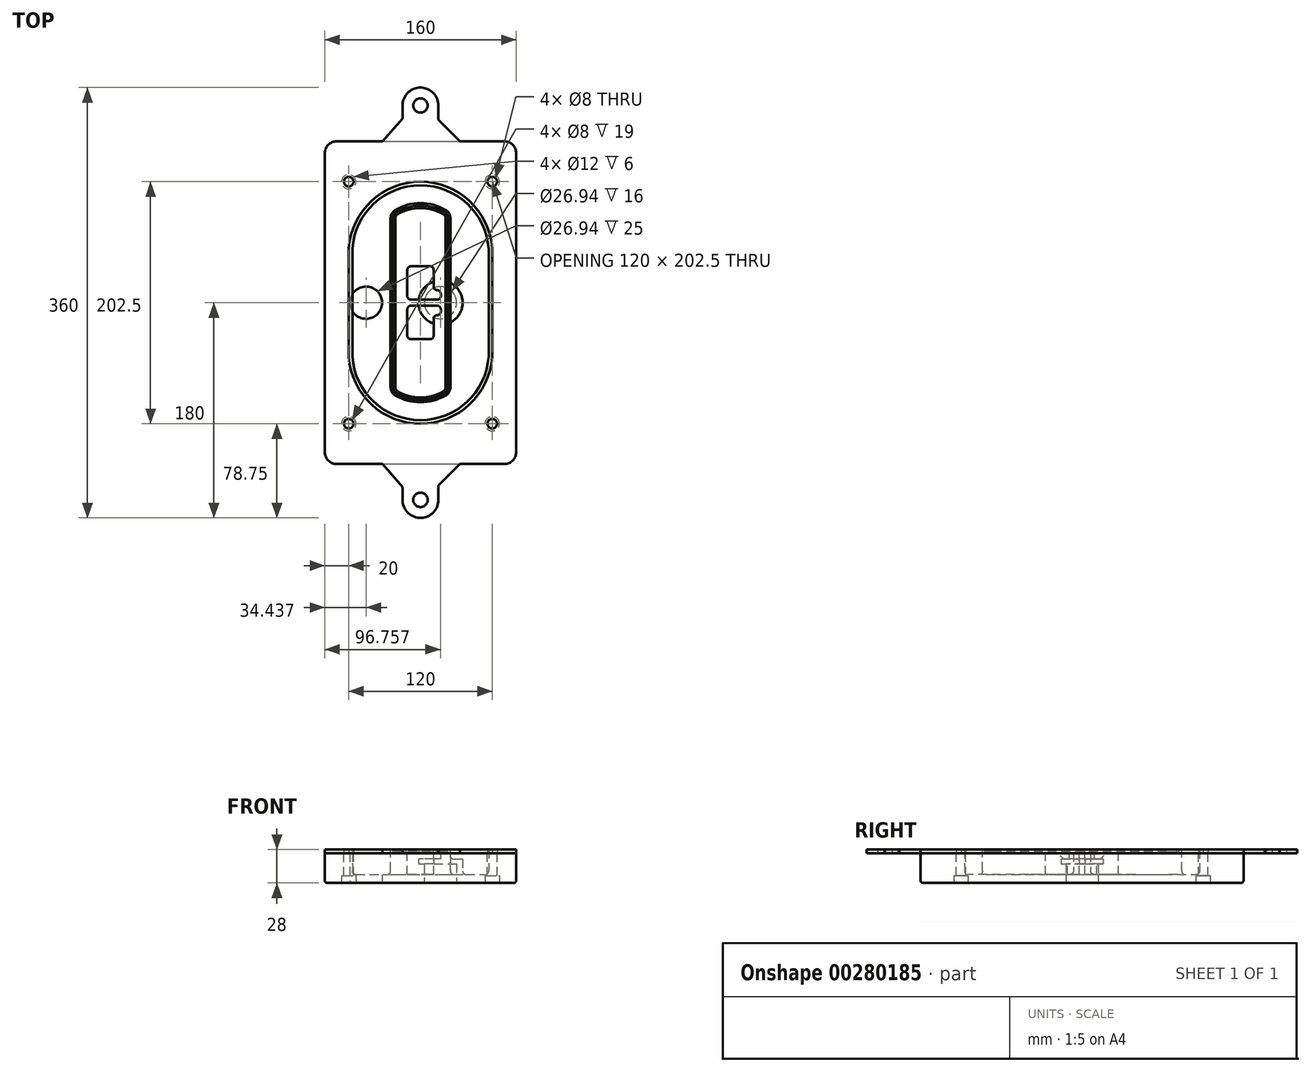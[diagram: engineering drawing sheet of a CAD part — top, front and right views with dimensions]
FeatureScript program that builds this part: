
annotation { "Feature Type Name" : "Feature", "Feature Type Description" : "" }
export const myFeature = defineFeature(function(context is Context, id is Id, definition is map)
    precondition{}
    {
        {
            var Q0;
            Q0=qCreatedBy(makeId("Top.planeOp"),FACE);
            var sketch = newSketch(context, id + "F0", { "sketchPlane" : qUnion([Q0])});
            skPoint(sketch, "E0.rect.middle", {"position": v(0, 0) * mm});
            skLineSegment(sketch, "E1.bottom", {"start": v(-70, -135) * mm, "end": v(70, -135) * mm});
            skLineSegment(sketch, "E1.top", {"start": v(-70, 135) * mm, "end": v(70, 135) * mm});
            skLineSegment(sketch, "E1.left", {"start": v(-80, -125) * mm, "end": v(-80, 125) * mm});
            skLineSegment(sketch, "E1.right", {"start": v(80, -125) * mm, "end": v(80, 125) * mm});
            skLineSegment(sketch, "E2", {"start": v(-80, 135) * mm, "end": v(80, -135) * mm, "construction": true});
            skLineSegment(sketch, "E3", {"start": v(80, 135) * mm, "end": v(-80, -135) * mm, "construction": true});
            skCircle(sketch, "E4", {"center": v(-60, 101.25) * mm, "radius": 4 * mm});
            skCircle(sketch, "E5", {"center": v(60, 101.25) * mm, "radius": 4 * mm});
            skCircle(sketch, "E6", {"center": v(60, -101.25) * mm, "radius": 4 * mm});
            skCircle(sketch, "E7", {"center": v(-60, -101.25) * mm, "radius": 4 * mm});
            skLineSegment(sketch, "E8", {"start": v(-60, 101.25) * mm, "end": v(60, 101.25) * mm, "construction": true});
            skLineSegment(sketch, "E9", {"start": v(60, 101.25) * mm, "end": v(60, -101.25) * mm, "construction": true});
            skLineSegment(sketch, "E10", {"start": v(60, -101.25) * mm, "end": v(-60, -101.25) * mm, "construction": true});
            skLineSegment(sketch, "E11", {"start": v(-60, -101.25) * mm, "end": v(-60, 101.25) * mm, "construction": true});
            skLineSegment(sketch, "E12", {"start": v(-60, 44.66) * mm, "end": v(-60, -44.66) * mm});
            skLineSegment(sketch, "E13", {"start": v(60, 44.66) * mm, "end": v(60, -44.66) * mm});
            skArc(sketch, "E14", {"start": v(59.98, 45.37) * mm, "mid": v(0, 101.25) * mm, "end": v(-59.98, 45.37) * mm});
            skArc(sketch, "E15", {"start": v(-59.98, -45.37) * mm, "mid": v(0, -101.25) * mm, "end": v(59.98, -45.37) * mm});
            skLineSegment(sketch, "E16", {"start": v(-60, 0) * mm, "end": v(60, 0) * mm, "construction": true});
            skPoint(sketch, "E17.visualSharp", {"position": v(-60, -45) * mm});
            skArc(sketch, "E17.filletArc", {"start": v(-60, -44.66) * mm, "mid": v(-60, -45.02) * mm, "end": v(-59.98, -45.37) * mm});
            skPoint(sketch, "E18.visualSharp", {"position": v(-60, 45) * mm});
            skArc(sketch, "E18.filletArc", {"start": v(-59.98, 45.37) * mm, "mid": v(-60, 45.02) * mm, "end": v(-60, 44.66) * mm});
            skPoint(sketch, "E19.visualSharp", {"position": v(60, 45) * mm});
            skArc(sketch, "E19.filletArc", {"start": v(60, 44.66) * mm, "mid": v(60, 45.02) * mm, "end": v(59.98, 45.37) * mm});
            skPoint(sketch, "E20.visualSharp", {"position": v(60, -45) * mm});
            skArc(sketch, "E20.filletArc", {"start": v(59.98, -45.37) * mm, "mid": v(60, -45.02) * mm, "end": v(60, -44.66) * mm});
            skPoint(sketch, "E21.visualSharp", {"position": v(-80, 135) * mm});
            skArc(sketch, "E21.filletArc", {"start": v(-70, 135) * mm, "mid": v(-77.07, 132.07) * mm, "end": v(-80, 125) * mm});
            skPoint(sketch, "E22.visualSharp", {"position": v(80, 135) * mm});
            skArc(sketch, "E22.filletArc", {"start": v(80, 125) * mm, "mid": v(77.07, 132.07) * mm, "end": v(70, 135) * mm});
            skPoint(sketch, "E23.visualSharp", {"position": v(80, -135) * mm});
            skArc(sketch, "E23.filletArc", {"start": v(70, -135) * mm, "mid": v(77.07, -132.07) * mm, "end": v(80, -125) * mm});
            skPoint(sketch, "E24.visualSharp", {"position": v(-80, -135) * mm});
            skArc(sketch, "E24.filletArc", {"start": v(-80, -125) * mm, "mid": v(-77.07, -132.07) * mm, "end": v(-70, -135) * mm});
            skArc(sketch, "E25.0", {"start": v(57, 44.66) * mm, "mid": v(57, 44.9) * mm, "end": v(56.98, 45.16) * mm});
            skLineSegment(sketch, "E25.1", {"start": v(57, 44.66) * mm, "end": v(57, -44.66) * mm});
            skArc(sketch, "E25.2", {"start": v(56.98, -45.16) * mm, "mid": v(57, -44.9) * mm, "end": v(57, -44.66) * mm});
            skArc(sketch, "E25.3", {"start": v(-56.98, -45.16) * mm, "mid": v(0, -98.25) * mm, "end": v(56.98, -45.16) * mm});
            skArc(sketch, "E25.4", {"start": v(-57, -44.66) * mm, "mid": v(-57, -44.9) * mm, "end": v(-56.98, -45.16) * mm});
            skArc(sketch, "E25.5", {"start": v(56.98, 45.16) * mm, "mid": v(0, 98.25) * mm, "end": v(-56.98, 45.16) * mm});
            skLineSegment(sketch, "E25.6", {"start": v(-57, 44.66) * mm, "end": v(-57, -44.66) * mm});
            skArc(sketch, "E25.7", {"start": v(-56.98, 45.16) * mm, "mid": v(-57, 44.9) * mm, "end": v(-57, 44.66) * mm});
            skArc(sketch, "E26.0", {"start": v(-63.97, 45.65) * mm, "mid": v(-64, 45.16) * mm, "end": v(-64, 44.66) * mm});
            skArc(sketch, "E26.1", {"start": v(63.97, 45.65) * mm, "mid": v(0, 105.25) * mm, "end": v(-63.97, 45.65) * mm});
            skArc(sketch, "E26.2", {"start": v(64, 44.66) * mm, "mid": v(64, 45.16) * mm, "end": v(63.97, 45.65) * mm});
            skLineSegment(sketch, "E26.3", {"start": v(64, 44.66) * mm, "end": v(64, -44.66) * mm});
            skArc(sketch, "E26.4", {"start": v(63.97, -45.65) * mm, "mid": v(64, -45.16) * mm, "end": v(64, -44.66) * mm});
            skLineSegment(sketch, "E26.5", {"start": v(-64, 44.66) * mm, "end": v(-64, -44.66) * mm});
            skArc(sketch, "E26.6", {"start": v(-63.97, -45.65) * mm, "mid": v(0, -105.25) * mm, "end": v(63.97, -45.65) * mm});
            skArc(sketch, "E26.7", {"start": v(-64, -44.66) * mm, "mid": v(-64, -45.16) * mm, "end": v(-63.97, -45.65) * mm});
            skSolve(sketch);
        }
        {
            var Q0;
            Q0=makeQuery(id+"F0.imprint","IMPRINT",FACE,{"disambiguationData":[TD([[makeQuery(id+"F0.imprint","IMPRINT",EDGE,{"derivedFrom":sQuery(id+"F0.wireOp",EDGE,"E1.bottom")}),1.0]])]});
            var Q1;
            Q1=makeQuery(id+"F0.imprint","IMPRINT",FACE,{"disambiguationData":[TD([[makeQuery(id+"F0.imprint","IMPRINT",EDGE,{"derivedFrom":sQuery(id+"F0.wireOp",EDGE,"E12")}),1.0]])]});
            var Q2;
            Q2=makeQuery(id+"F0.imprint","IMPRINT",FACE,{"disambiguationData":[TD([[makeQuery(id+"F0.imprint","IMPRINT",EDGE,{"derivedFrom":sQuery(id+"F0.wireOp",EDGE,"E25.0")}),1.0]])]});
            var Q3;
            Q3=makeQuery(id+"F0.imprint","IMPRINT",FACE,{"disambiguationData":[TD([[makeQuery(id+"F0.imprint","IMPRINT",EDGE,{"derivedFrom":sQuery(id+"F0.wireOp",EDGE,"E12")}),-1.0]])]});
            extrude(context, id + "F1", {"entities" : qUnion([Q0, Q1, Q2, Q3]), "oppositeDirection" : true, "depth" : 25 * mm});
        }
        {
            var Q0;
            Q0=makeQuery(id+"F0.imprint","IMPRINT",FACE,{"disambiguationData":[TD([[makeQuery(id+"F0.imprint","IMPRINT",EDGE,{"derivedFrom":sQuery(id+"F0.wireOp",EDGE,"E12")}),1.0]])]});
            extrude(context, id + "F2", {"entities" : qUnion([Q0]), "operationType" : NewBodyOperationType.ADD, "depth" : 3 * mm});
        }
        {
            var Q0;
            Q0=makeQuery(id+"F0.imprint","IMPRINT",FACE,{"disambiguationData":[TD([[makeQuery(id+"F0.imprint","IMPRINT",EDGE,{"derivedFrom":sQuery(id+"F0.wireOp",EDGE,"E25.0")}),1.0]])]});
            extrude(context, id + "F3", {"entities" : qUnion([Q0]), "operationType" : NewBodyOperationType.REMOVE, "oppositeDirection" : true, "depth" : 18 * mm});
        }
        {
            var Q0;
            Q0=makeQuery(id+"F2.opExtrude","CAP_FACE",FACE,{"disambiguationData":[OSD([sQuery(id+"F0.wireOp",EDGE,"E12"),sQuery(id+"F0.wireOp",EDGE,"E13"),sQuery(id+"F0.wireOp",EDGE,"E14"),sQuery(id+"F0.wireOp",EDGE,"E15"),sQuery(id+"F0.wireOp",EDGE,"E17.filletArc"),sQuery(id+"F0.wireOp",EDGE,"E18.filletArc"),sQuery(id+"F0.wireOp",EDGE,"E19.filletArc"),sQuery(id+"F0.wireOp",EDGE,"E20.filletArc"),sQuery(id+"F0.wireOp",EDGE,"E25.0"),sQuery(id+"F0.wireOp",EDGE,"E25.1"),sQuery(id+"F0.wireOp",EDGE,"E25.2"),sQuery(id+"F0.wireOp",EDGE,"E25.3"),sQuery(id+"F0.wireOp",EDGE,"E25.4"),sQuery(id+"F0.wireOp",EDGE,"E25.5"),sQuery(id+"F0.wireOp",EDGE,"E25.6"),sQuery(id+"F0.wireOp",EDGE,"E25.7")])],"isStart":false});
            var sketch = newSketch(context, id + "F4", { "sketchPlane" : qUnion([Q0])});
            skArc(sketch, "E27.0", {"start": v(-20.99, -77.65) * mm, "mid": v(0, -83.25) * mm, "end": v(20.99, -77.65) * mm});
            skArc(sketch, "E28.0", {"start": v(20.99, 77.65) * mm, "mid": v(0, 83.25) * mm, "end": v(-20.99, 77.65) * mm});
            skLineSegment(sketch, "E29", {"start": v(-25, 70.71) * mm, "end": v(-25, -70.71) * mm});
            skLineSegment(sketch, "E30", {"start": v(25, 70.71) * mm, "end": v(25, -70.71) * mm});
            skLineSegment(sketch, "E31", {"start": v(-25, 75.03) * mm, "end": v(25, 75.03) * mm, "construction": true});
            skLineSegment(sketch, "E32", {"start": v(-25, -75.03) * mm, "end": v(25, -75.03) * mm, "construction": true});
            skPoint(sketch, "E33.visualSharp", {"position": v(-25, 75.03) * mm});
            skArc(sketch, "E33.filletArc", {"start": v(-20.99, 77.65) * mm, "mid": v(-23.92, 74.72) * mm, "end": v(-25, 70.71) * mm});
            skPoint(sketch, "E34.visualSharp", {"position": v(25, 75.03) * mm});
            skArc(sketch, "E34.filletArc", {"start": v(25, 70.71) * mm, "mid": v(23.92, 74.72) * mm, "end": v(20.99, 77.65) * mm});
            skPoint(sketch, "E35.visualSharp", {"position": v(25, -75.03) * mm});
            skArc(sketch, "E35.filletArc", {"start": v(20.99, -77.65) * mm, "mid": v(23.92, -74.72) * mm, "end": v(25, -70.71) * mm});
            skPoint(sketch, "E36.visualSharp", {"position": v(-25, -75.03) * mm});
            skArc(sketch, "E36.filletArc", {"start": v(-25, -70.71) * mm, "mid": v(-23.92, -74.72) * mm, "end": v(-20.99, -77.65) * mm});
            skArc(sketch, "E37.0", {"start": v(56.98, 45.16) * mm, "mid": v(0, 98.25) * mm, "end": v(-56.98, 45.16) * mm});
            skArc(sketch, "E37.1", {"start": v(-56.98, 45.16) * mm, "mid": v(-57, 44.9) * mm, "end": v(-57, 44.66) * mm});
            skLineSegment(sketch, "E37.2", {"start": v(-57, 44.66) * mm, "end": v(-57, -44.66) * mm});
            skArc(sketch, "E37.3", {"start": v(-57, -44.66) * mm, "mid": v(-57, -44.9) * mm, "end": v(-56.98, -45.16) * mm});
            skArc(sketch, "E37.4", {"start": v(-56.98, -45.16) * mm, "mid": v(0, -98.25) * mm, "end": v(56.98, -45.16) * mm});
            skArc(sketch, "E37.5", {"start": v(56.98, -45.16) * mm, "mid": v(57, -44.9) * mm, "end": v(57, -44.66) * mm});
            skLineSegment(sketch, "E37.6", {"start": v(57, 44.66) * mm, "end": v(57, -44.66) * mm});
            skArc(sketch, "E37.7", {"start": v(57, 44.66) * mm, "mid": v(57, 44.9) * mm, "end": v(56.98, 45.16) * mm});
            skLineSegment(sketch, "E38.0", {"start": v(23, 70.71) * mm, "end": v(23, -70.71) * mm});
            skArc(sketch, "E38.1", {"start": v(19.99, -75.92) * mm, "mid": v(22.2, -73.72) * mm, "end": v(23, -70.71) * mm});
            skArc(sketch, "E38.2", {"start": v(-19.99, -75.92) * mm, "mid": v(0, -81.25) * mm, "end": v(19.99, -75.92) * mm});
            skArc(sketch, "E38.3", {"start": v(-23, -70.71) * mm, "mid": v(-22.2, -73.72) * mm, "end": v(-19.99, -75.92) * mm});
            skLineSegment(sketch, "E38.4", {"start": v(-23, 70.71) * mm, "end": v(-23, -70.71) * mm});
            skArc(sketch, "E38.5", {"start": v(23, 70.71) * mm, "mid": v(22.2, 73.72) * mm, "end": v(19.99, 75.92) * mm});
            skArc(sketch, "E38.6", {"start": v(-19.99, 75.92) * mm, "mid": v(-22.2, 73.72) * mm, "end": v(-23, 70.71) * mm});
            skArc(sketch, "E38.7", {"start": v(19.99, 75.92) * mm, "mid": v(0, 81.25) * mm, "end": v(-19.99, 75.92) * mm});
            skArc(sketch, "E39.0", {"start": v(21, 70.71) * mm, "mid": v(20.46, 72.72) * mm, "end": v(19, 74.18) * mm});
            skLineSegment(sketch, "E39.1", {"start": v(21, 70.71) * mm, "end": v(21, -70.71) * mm});
            skArc(sketch, "E39.2", {"start": v(19, -74.18) * mm, "mid": v(20.46, -72.72) * mm, "end": v(21, -70.71) * mm});
            skArc(sketch, "E39.3", {"start": v(-19, -74.18) * mm, "mid": v(0, -79.25) * mm, "end": v(19, -74.18) * mm});
            skArc(sketch, "E39.4", {"start": v(-21, -70.71) * mm, "mid": v(-20.46, -72.72) * mm, "end": v(-19, -74.18) * mm});
            skArc(sketch, "E39.5", {"start": v(19, 74.18) * mm, "mid": v(0, 79.25) * mm, "end": v(-19, 74.18) * mm});
            skLineSegment(sketch, "E39.6", {"start": v(-21, 70.71) * mm, "end": v(-21, -70.71) * mm});
            skArc(sketch, "E39.7", {"start": v(-19, 74.18) * mm, "mid": v(-20.46, 72.72) * mm, "end": v(-21, 70.71) * mm});
            skLineSegment(sketch, "E40", {"start": v(-25, 0) * mm, "end": v(25, 0) * mm, "construction": true});
            skLineSegment(sketch, "E41", {"start": v(-11, 5.5) * mm, "end": v(-11, 27.5) * mm});
            skLineSegment(sketch, "E42", {"start": v(-8, 30.5) * mm, "end": v(8, 30.5) * mm});
            skLineSegment(sketch, "E43", {"start": v(11, 27.5) * mm, "end": v(11, 13.5) * mm});
            skLineSegment(sketch, "E44", {"start": v(14, 10.5) * mm, "end": v(14, 10.5) * mm});
            skLineSegment(sketch, "E45", {"start": v(17, 7.5) * mm, "end": v(17, 5.5) * mm});
            skLineSegment(sketch, "E46", {"start": v(14, 2.5) * mm, "end": v(-8, 2.5) * mm});
            skPoint(sketch, "E47.visualSharp", {"position": v(-11, 30.5) * mm});
            skArc(sketch, "E47.filletArc", {"start": v(-8, 30.5) * mm, "mid": v(-10.12, 29.62) * mm, "end": v(-11, 27.5) * mm});
            skPoint(sketch, "E48.visualSharp", {"position": v(11, 30.5) * mm});
            skArc(sketch, "E48.filletArc", {"start": v(11, 27.5) * mm, "mid": v(10.12, 29.62) * mm, "end": v(8, 30.5) * mm});
            skPoint(sketch, "E49.visualSharp", {"position": v(11, 10.5) * mm});
            skArc(sketch, "E49.filletArc", {"start": v(11, 13.5) * mm, "mid": v(11.88, 11.38) * mm, "end": v(14, 10.5) * mm});
            skPoint(sketch, "E50.visualSharp", {"position": v(17, 10.5) * mm});
            skArc(sketch, "E50.filletArc", {"start": v(17, 7.5) * mm, "mid": v(16.12, 9.62) * mm, "end": v(14, 10.5) * mm});
            skPoint(sketch, "E51.visualSharp", {"position": v(17, 2.5) * mm});
            skArc(sketch, "E51.filletArc", {"start": v(14, 2.5) * mm, "mid": v(16.12, 3.38) * mm, "end": v(17, 5.5) * mm});
            skPoint(sketch, "E52.visualSharp", {"position": v(-11, 2.5) * mm});
            skArc(sketch, "E52.filletArc", {"start": v(-11, 5.5) * mm, "mid": v(-10.12, 3.38) * mm, "end": v(-8, 2.5) * mm});
            skLineSegment(sketch, "E53.0.MirrorCS", {"start": v(14, -2.5) * mm, "end": v(-8, -2.5) * mm});
            skArc(sketch, "E54.0.MirrorCS", {"start": v(-11, -5.5) * mm, "mid": v(-10.12, -3.38) * mm, "end": v(-8, -2.5) * mm});
            skLineSegment(sketch, "E55.0.MirrorCS", {"start": v(-11, -5.5) * mm, "end": v(-11, -27.5) * mm});
            skArc(sketch, "E56.0.MirrorCS", {"start": v(-8, -30.5) * mm, "mid": v(-10.12, -29.62) * mm, "end": v(-11, -27.5) * mm});
            skLineSegment(sketch, "E57.0.MirrorCS", {"start": v(-8, -30.5) * mm, "end": v(8, -30.5) * mm});
            skArc(sketch, "E58.0.MirrorCS", {"start": v(11, -27.5) * mm, "mid": v(10.12, -29.62) * mm, "end": v(8, -30.5) * mm});
            skLineSegment(sketch, "E59.0.MirrorCS", {"start": v(11, -27.5) * mm, "end": v(11, -13.5) * mm});
            skArc(sketch, "E60.0.MirrorCS", {"start": v(11, -13.5) * mm, "mid": v(11.88, -11.38) * mm, "end": v(14, -10.5) * mm});
            skArc(sketch, "E61.0.MirrorCS", {"start": v(17, -7.5) * mm, "mid": v(16.12, -9.62) * mm, "end": v(14, -10.5) * mm});
            skLineSegment(sketch, "E62.0.MirrorCS", {"start": v(17, -7.5) * mm, "end": v(17, -5.5) * mm});
            skArc(sketch, "E63.0.MirrorCS", {"start": v(14, -2.5) * mm, "mid": v(16.12, -3.38) * mm, "end": v(17, -5.5) * mm});
            skSolve(sketch);
        }
        {
            var Q0;
            Q0=makeQuery(id+"F4.imprint","IMPRINT",FACE,{"disambiguationData":[TD([[makeQuery(id+"F4.imprint","IMPRINT",EDGE,{"derivedFrom":sQuery(id+"F4.wireOp",EDGE,"E27.0")}),1.0]])]});
            var Q1;
            Q1=makeQuery(id+"F4.imprint","IMPRINT",FACE,{"disambiguationData":[TD([[makeQuery(id+"F4.imprint","IMPRINT",EDGE,{"derivedFrom":sQuery(id+"F4.wireOp",EDGE,"E38.0")}),-1.0]])]});
            var Q2;
            Q2=makeQuery(id+"F4.imprint","IMPRINT",FACE,{"disambiguationData":[TD([[makeQuery(id+"F4.imprint","IMPRINT",EDGE,{"derivedFrom":sQuery(id+"F4.wireOp",EDGE,"E39.0")}),1.0]])]});
            extrude(context, id + "F5", {"entities" : qUnion([Q0, Q1, Q2]), "operationType" : NewBodyOperationType.ADD, "endBound" : BoundingType.UP_TO_NEXT, "oppositeDirection" : true, "depth" : 25 * mm});
        }
        {
            var Q0;
            Q0=makeQuery(id+"F4.imprint","IMPRINT",FACE,{"disambiguationData":[TD([[makeQuery(id+"F4.imprint","IMPRINT",EDGE,{"derivedFrom":sQuery(id+"F4.wireOp",EDGE,"E38.0")}),-1.0]])]});
            extrude(context, id + "F6", {"entities" : qUnion([Q0]), "operationType" : NewBodyOperationType.REMOVE, "oppositeDirection" : true, "depth" : 2 * mm});
        }
        {
            var Q0;
            Q0=makeQuery(id+"F1.opExtrude","CAP_FACE",FACE,{"disambiguationData":[OSD([sQuery(id+"F0.wireOp",EDGE,"E1.bottom"),sQuery(id+"F0.wireOp",EDGE,"E1.top"),sQuery(id+"F0.wireOp",EDGE,"E1.left"),sQuery(id+"F0.wireOp",EDGE,"E1.right"),sQuery(id+"F0.wireOp",EDGE,"E4"),sQuery(id+"F0.wireOp",EDGE,"E5"),sQuery(id+"F0.wireOp",EDGE,"E6"),sQuery(id+"F0.wireOp",EDGE,"E7"),sQuery(id+"F0.wireOp",EDGE,"E21.filletArc"),sQuery(id+"F0.wireOp",EDGE,"E22.filletArc"),sQuery(id+"F0.wireOp",EDGE,"E23.filletArc"),sQuery(id+"F0.wireOp",EDGE,"E24.filletArc")])],"isStart":false});
            var sketch = newSketch(context, id + "F7", { "sketchPlane" : qUnion([Q0])});
            skCircle(sketch, "E64", {"center": v(16.76, 0) * mm, "radius": 13.47 * mm});
            skCircle(sketch, "E65", {"center": v(-45.56, 0) * mm, "radius": 13.47 * mm});
            skLineSegment(sketch, "E66", {"start": v(80, 0) * mm, "end": v(-80, 0) * mm});
            skCircle(sketch, "E67", {"center": v(16.76, 0) * mm, "radius": 18.47 * mm});
            skCircle(sketch, "E68", {"center": v(60, -101.25) * mm, "radius": 6 * mm});
            skCircle(sketch, "E69", {"center": v(-60, -101.25) * mm, "radius": 6 * mm});
            skCircle(sketch, "E70", {"center": v(-60, 101.25) * mm, "radius": 6 * mm});
            skCircle(sketch, "E71", {"center": v(60, 101.25) * mm, "radius": 6 * mm});
            skSolve(sketch);
        }
        {
            var Q0;
            {var subQ1=sQuery(id+"F7.wireOp",EDGE,"E66");var subQ4=sQuery(id+"F7.wireOp",EDGE,"E64");var subQ6=makeQuery(id+"F7.imprint","INTERSECT",VERTEX,{"disambiguationData":[OD(0.0)],"derivedFrom":[subQ4,subQ1]});Q0=makeQuery(id+"F7.imprint","IMPRINT",FACE,{"disambiguationData":[TD([[makeQuery(id+"F7.imprint","IMPRINT",EDGE,{"disambiguationData":[TD([[subQ6,-1.0]])],"derivedFrom":subQ4}),-1.0]])]});}
            var Q1;
            {var subQ0=sQuery(id+"F7.wireOp",EDGE,"E66");var subQ1=sQuery(id+"F7.wireOp",EDGE,"E64");var subQ3=makeQuery(id+"F7.imprint","INTERSECT",VERTEX,{"disambiguationData":[OD(0.0)],"derivedFrom":[subQ1,subQ0]});Q1=makeQuery(id+"F7.imprint","IMPRINT",FACE,{"disambiguationData":[TD([[makeQuery(id+"F7.imprint","IMPRINT",EDGE,{"disambiguationData":[TD([[subQ3,-1.0]])],"derivedFrom":subQ1}),1.0]])]});}
            var Q2;
            {var subQ0=sQuery(id+"F7.wireOp",EDGE,"E66");var subQ1=sQuery(id+"F7.wireOp",EDGE,"E64");var subQ3=makeQuery(id+"F7.imprint","INTERSECT",VERTEX,{"disambiguationData":[OD(0.0)],"derivedFrom":[subQ1,subQ0]});Q2=makeQuery(id+"F7.imprint","IMPRINT",FACE,{"disambiguationData":[TD([[makeQuery(id+"F7.imprint","IMPRINT",EDGE,{"disambiguationData":[TD([[subQ3,1.0]])],"derivedFrom":subQ1}),1.0]])]});}
            var Q3;
            {var subQ1=sQuery(id+"F7.wireOp",EDGE,"E66");var subQ4=sQuery(id+"F7.wireOp",EDGE,"E64");var subQ6=makeQuery(id+"F7.imprint","INTERSECT",VERTEX,{"disambiguationData":[OD(0.0)],"derivedFrom":[subQ4,subQ1]});Q3=makeQuery(id+"F7.imprint","IMPRINT",FACE,{"disambiguationData":[TD([[makeQuery(id+"F7.imprint","IMPRINT",EDGE,{"disambiguationData":[TD([[subQ6,1.0]])],"derivedFrom":subQ4}),-1.0]])]});}
            extrude(context, id + "F8", {"entities" : qUnion([Q0, Q1, Q2, Q3]), "operationType" : NewBodyOperationType.ADD, "oppositeDirection" : true, "depth" : 20 * mm});
        }
        {
            var Q0;
            {var subQ0=sQuery(id+"F7.wireOp",EDGE,"E66");var subQ1=sQuery(id+"F7.wireOp",EDGE,"E64");var subQ3=makeQuery(id+"F7.imprint","INTERSECT",VERTEX,{"disambiguationData":[OD(0.0)],"derivedFrom":[subQ1,subQ0]});Q0=makeQuery(id+"F7.imprint","IMPRINT",FACE,{"disambiguationData":[TD([[makeQuery(id+"F7.imprint","IMPRINT",EDGE,{"disambiguationData":[TD([[subQ3,-1.0]])],"derivedFrom":subQ1}),1.0]])]});}
            var Q1;
            {var subQ0=sQuery(id+"F7.wireOp",EDGE,"E66");var subQ1=sQuery(id+"F7.wireOp",EDGE,"E64");var subQ3=makeQuery(id+"F7.imprint","INTERSECT",VERTEX,{"disambiguationData":[OD(0.0)],"derivedFrom":[subQ1,subQ0]});Q1=makeQuery(id+"F7.imprint","IMPRINT",FACE,{"disambiguationData":[TD([[makeQuery(id+"F7.imprint","IMPRINT",EDGE,{"disambiguationData":[TD([[subQ3,1.0]])],"derivedFrom":subQ1}),1.0]])]});}
            extrude(context, id + "F9", {"entities" : qUnion([Q0, Q1]), "operationType" : NewBodyOperationType.REMOVE, "oppositeDirection" : true, "depth" : 16 * mm});
        }
        {
            var Q0;
            {var subQ0=sQuery(id+"F7.wireOp",EDGE,"E66");var subQ1=sQuery(id+"F7.wireOp",EDGE,"E65");var subQ3=makeQuery(id+"F7.imprint","INTERSECT",VERTEX,{"disambiguationData":[OD(0.0)],"derivedFrom":[subQ1,subQ0]});Q0=makeQuery(id+"F7.imprint","IMPRINT",FACE,{"disambiguationData":[TD([[makeQuery(id+"F7.imprint","IMPRINT",EDGE,{"disambiguationData":[TD([[subQ3,-1.0]])],"derivedFrom":subQ1}),1.0]])]});}
            var Q1;
            {var subQ0=sQuery(id+"F7.wireOp",EDGE,"E66");var subQ1=sQuery(id+"F7.wireOp",EDGE,"E65");var subQ3=makeQuery(id+"F7.imprint","INTERSECT",VERTEX,{"disambiguationData":[OD(0.0)],"derivedFrom":[subQ1,subQ0]});Q1=makeQuery(id+"F7.imprint","IMPRINT",FACE,{"disambiguationData":[TD([[makeQuery(id+"F7.imprint","IMPRINT",EDGE,{"disambiguationData":[TD([[subQ3,1.0]])],"derivedFrom":subQ1}),1.0]])]});}
            extrude(context, id + "F10", {"entities" : qUnion([Q0, Q1]), "operationType" : NewBodyOperationType.REMOVE, "oppositeDirection" : true, "depth" : 25 * mm});
        }
        {
            var Q0;
            Q0=makeQuery(id+"F7.imprint","IMPRINT",FACE,{"disambiguationData":[TD([[makeQuery(id+"F7.imprint","IMPRINT",EDGE,{"derivedFrom":sQuery(id+"F7.wireOp",EDGE,"E68")}),1.0]])]});
            var Q1;
            Q1=makeQuery(id+"F7.imprint","IMPRINT",FACE,{"disambiguationData":[TD([[makeQuery(id+"F7.imprint","IMPRINT",EDGE,{"derivedFrom":makeQuery(id+"F1.opExtrude","CAP_EDGE",EDGE,{"disambiguationData":[OSD([sQuery(id+"F0.wireOp",EDGE,"E5")])],"isStart":false})}),-1.0]])]});
            var Q2;
            Q2=makeQuery(id+"F7.imprint","IMPRINT",FACE,{"disambiguationData":[TD([[makeQuery(id+"F7.imprint","IMPRINT",EDGE,{"derivedFrom":sQuery(id+"F7.wireOp",EDGE,"E69")}),1.0]])]});
            var Q3;
            Q3=makeQuery(id+"F7.imprint","IMPRINT",FACE,{"disambiguationData":[TD([[makeQuery(id+"F7.imprint","IMPRINT",EDGE,{"derivedFrom":makeQuery(id+"F1.opExtrude","CAP_EDGE",EDGE,{"disambiguationData":[OSD([sQuery(id+"F0.wireOp",EDGE,"E4")])],"isStart":false})}),-1.0]])]});
            var Q4;
            Q4=makeQuery(id+"F7.imprint","IMPRINT",FACE,{"disambiguationData":[TD([[makeQuery(id+"F7.imprint","IMPRINT",EDGE,{"derivedFrom":sQuery(id+"F7.wireOp",EDGE,"E70")}),1.0]])]});
            var Q5;
            Q5=makeQuery(id+"F7.imprint","IMPRINT",FACE,{"disambiguationData":[TD([[makeQuery(id+"F7.imprint","IMPRINT",EDGE,{"derivedFrom":makeQuery(id+"F1.opExtrude","CAP_EDGE",EDGE,{"disambiguationData":[OSD([sQuery(id+"F0.wireOp",EDGE,"E7")])],"isStart":false})}),-1.0]])]});
            var Q6;
            Q6=makeQuery(id+"F7.imprint","IMPRINT",FACE,{"disambiguationData":[TD([[makeQuery(id+"F7.imprint","IMPRINT",EDGE,{"derivedFrom":sQuery(id+"F7.wireOp",EDGE,"E71")}),1.0]])]});
            var Q7;
            Q7=makeQuery(id+"F7.imprint","IMPRINT",FACE,{"disambiguationData":[TD([[makeQuery(id+"F7.imprint","IMPRINT",EDGE,{"derivedFrom":makeQuery(id+"F1.opExtrude","CAP_EDGE",EDGE,{"disambiguationData":[OSD([sQuery(id+"F0.wireOp",EDGE,"E6")])],"isStart":false})}),-1.0]])]});
            extrude(context, id + "F11", {"entities" : qUnion([Q0, Q1, Q2, Q3, Q4, Q5, Q6, Q7]), "operationType" : NewBodyOperationType.REMOVE, "oppositeDirection" : true, "depth" : 6 * mm});
        }
        {
            var Q0;
            Q0=makeQuery(id+"F9.boolean.opBoolean","COPY",FACE,{"derivedFrom":makeQuery(id+"F9.opExtrude","CAP_FACE",FACE,{"disambiguationData":[OSD([sQuery(id+"F7.wireOp",EDGE,"E64")])],"isStart":false})});
            var sketch = newSketch(context, id + "F12", { "sketchPlane" : qUnion([Q0])});
            skArc(sketch, "E72.0", {"start": v(11, 17.55) * mm, "mid": v(2.57, 11.82) * mm, "end": v(-1.54, 2.5) * mm});
            skArc(sketch, "E72.1", {"start": v(-1.54, -2.5) * mm, "mid": v(2.57, -11.82) * mm, "end": v(11, -17.55) * mm});
            skLineSegment(sketch, "E73", {"start": v(-1.54, -2.5) * mm, "end": v(14, -2.5) * mm});
            skLineSegment(sketch, "E74.0", {"start": v(14, 2.5) * mm, "end": v(-1.54, 2.5) * mm});
            skArc(sketch, "E74.1", {"start": v(14, 2.5) * mm, "mid": v(16.12, 3.38) * mm, "end": v(17, 5.5) * mm});
            skLineSegment(sketch, "E74.2", {"start": v(17, 7.5) * mm, "end": v(17, 5.5) * mm});
            skArc(sketch, "E74.3", {"start": v(17, 7.5) * mm, "mid": v(16.12, 9.62) * mm, "end": v(14, 10.5) * mm});
            skArc(sketch, "E74.4", {"start": v(11, 13.5) * mm, "mid": v(11.88, 11.38) * mm, "end": v(14, 10.5) * mm});
            skLineSegment(sketch, "E74.5", {"start": v(11, 17.55) * mm, "end": v(11, 13.5) * mm});
            skLineSegment(sketch, "E74.7", {"start": v(14, -2.5) * mm, "end": v(-1.54, -2.5) * mm});
            skArc(sketch, "E74.8", {"start": v(14, -2.5) * mm, "mid": v(16.12, -3.38) * mm, "end": v(17, -5.5) * mm});
            skLineSegment(sketch, "E74.9", {"start": v(17, -7.5) * mm, "end": v(17, -5.5) * mm});
            skArc(sketch, "E74.10", {"start": v(17, -7.5) * mm, "mid": v(16.12, -9.62) * mm, "end": v(14, -10.5) * mm});
            skArc(sketch, "E74.11", {"start": v(11, -13.5) * mm, "mid": v(11.88, -11.38) * mm, "end": v(14, -10.5) * mm});
            skLineSegment(sketch, "E74.12", {"start": v(11, -17.55) * mm, "end": v(11, -13.5) * mm});
            skPoint(sketch, "E75.orphan", {"position": v(11, -27.5) * mm});
            skPoint(sketch, "E76.orphan", {"position": v(-8, -2.5) * mm});
            skPoint(sketch, "E77.orphan", {"position": v(-8, 2.5) * mm});
            skPoint(sketch, "E78.orphan", {"position": v(11, 27.5) * mm});
            skSolve(sketch);
        }
        {
            var Q0;
            {var subQ7=sQuery(id+"F12.wireOp",EDGE,"E72.0");var subQ14=sQuery(id+"F12.wireOp",EDGE,"E72.1");var subQ16=sQuery(id+"F12.wireOp",EDGE,"E74.1");var subQ18=sQuery(id+"F12.wireOp",EDGE,"E74.8");Q0=qUnion([makeQuery(id+"F12.imprint","IMPRINT",FACE,{"disambiguationData":[TD([[makeQuery(id+"F12.imprint","IMPRINT",EDGE,{"derivedFrom":subQ7}),1.0]])]}),makeQuery(id+"F12.imprint","IMPRINT",FACE,{"disambiguationData":[TD([[makeQuery(id+"F12.imprint","IMPRINT",EDGE,{"derivedFrom":subQ14}),1.0]])]}),makeQuery(id+"F12.imprint","IMPRINT",FACE,{"disambiguationData":[TD([[makeQuery(id+"F12.imprint","IMPRINT",EDGE,{"derivedFrom":subQ16}),1.0]])]}),makeQuery(id+"F12.imprint","IMPRINT",FACE,{"disambiguationData":[TD([[makeQuery(id+"F12.imprint","IMPRINT",EDGE,{"derivedFrom":subQ18}),-1.0]])]})]);}
            var Q1;
            Q1=makeQuery(id+"F5.boolean.opBoolean","SPLIT",FACE,{"disambiguationData":[TD([makeQuery(id+"F5.opExtrude","SWEPT_FACE",FACE,{"disambiguationData":[OSD([sQuery(id+"F4.wireOp",EDGE,"E41")])]})])],"derivedFrom":makeQuery(id+"F3.boolean.opBoolean","COPY",FACE,{"derivedFrom":makeQuery(id+"F3.opExtrude","CAP_FACE",FACE,{"disambiguationData":[OSD([sQuery(id+"F0.wireOp",EDGE,"E25.0"),sQuery(id+"F0.wireOp",EDGE,"E25.1"),sQuery(id+"F0.wireOp",EDGE,"E25.2"),sQuery(id+"F0.wireOp",EDGE,"E25.3"),sQuery(id+"F0.wireOp",EDGE,"E25.4"),sQuery(id+"F0.wireOp",EDGE,"E25.5"),sQuery(id+"F0.wireOp",EDGE,"E25.6"),sQuery(id+"F0.wireOp",EDGE,"E25.7")])],"isStart":false})})});
            extrude(context, id + "F13", {"entities" : qUnion([Q0]), "operationType" : NewBodyOperationType.REMOVE, "endBound" : BoundingType.UP_TO_SURFACE, "endBoundEntityFace" : qUnion([Q1]), "depth" : 25 * mm});
        }
        {
            var Q0;
            Q0=makeQuery(id+"F3.boolean.opBoolean","COPY",EDGE,{"derivedFrom":makeQuery(id+"F3.opExtrude","CAP_EDGE",EDGE,{"disambiguationData":[OSD([sQuery(id+"F0.wireOp",EDGE,"E25.6")])],"isStart":false})});
            var Q1;
            Q1=makeQuery(id+"F8.boolean.opBoolean","INTERSECT",EDGE,{"derivedFrom":[makeQuery(id+"F5.opExtrude","SWEPT_FACE",FACE,{"disambiguationData":[OSD([sQuery(id+"F4.wireOp",EDGE,"E30")])]}),makeQuery(id+"F8.opExtrude","CAP_FACE",FACE,{"disambiguationData":[OSD([sQuery(id+"F7.wireOp",EDGE,"E67")])],"isStart":false})]});
            var Q2;
            Q2=makeQuery(id+"F8.boolean.opBoolean","INTERSECT",EDGE,{"disambiguationData":[OD(1.0)],"derivedFrom":[makeQuery(id+"F5.opExtrude","SWEPT_FACE",FACE,{"disambiguationData":[OSD([sQuery(id+"F4.wireOp",EDGE,"E30")])]}),makeQuery(id+"F8.opExtrude","SWEPT_FACE",FACE,{"disambiguationData":[OSD([sQuery(id+"F7.wireOp",EDGE,"E67")])]})]});
            var Q3;
            {var subQ0=sQuery(id+"F4.wireOp",EDGE,"E30");Q3=makeQuery(id+"F8.boolean.opBoolean","SPLIT",EDGE,{"disambiguationData":[TD([makeQuery(id+"F5.opExtrude","SWEPT_FACE",FACE,{"disambiguationData":[OSD([sQuery(id+"F4.wireOp",EDGE,"E35.filletArc")])]})])],"derivedFrom":makeQuery(id+"F5.opExtrude","CAP_EDGE",EDGE,{"disambiguationData":[OSD([subQ0])],"isStart":false})});}
            var Q4;
            {var subQ0=sQuery(id+"F0.wireOp",EDGE,"E25.7");var subQ1=sQuery(id+"F0.wireOp",EDGE,"E25.1");var subQ2=sQuery(id+"F0.wireOp",EDGE,"E25.6");var subQ3=sQuery(id+"F0.wireOp",EDGE,"E25.5");var subQ4=sQuery(id+"F0.wireOp",EDGE,"E25.4");var subQ5=sQuery(id+"F0.wireOp",EDGE,"E25.0");var subQ6=sQuery(id+"F0.wireOp",EDGE,"E25.2");var subQ7=sQuery(id+"F0.wireOp",EDGE,"E25.3");Q4=makeQuery(id+"F8.boolean.opBoolean","INTERSECT",EDGE,{"derivedFrom":[makeQuery(id+"F5.boolean.opBoolean","SPLIT",FACE,{"disambiguationData":[TD([makeQuery(id+"F2.opExtrude","SWEPT_FACE",FACE,{"disambiguationData":[OSD([subQ5])]})])],"derivedFrom":makeQuery(id+"F3.boolean.opBoolean","COPY",FACE,{"derivedFrom":makeQuery(id+"F3.opExtrude","CAP_FACE",FACE,{"disambiguationData":[OSD([subQ5,subQ1,subQ6,subQ7,subQ4,subQ3,subQ2,subQ0])],"isStart":false})})}),makeQuery(id+"F8.opExtrude","SWEPT_FACE",FACE,{"disambiguationData":[OSD([sQuery(id+"F7.wireOp",EDGE,"E67")])]})]});}
            var Q5;
            Q5=makeQuery(id+"F8.boolean.opBoolean","INTERSECT",EDGE,{"disambiguationData":[OD(0.0)],"derivedFrom":[makeQuery(id+"F5.opExtrude","SWEPT_FACE",FACE,{"disambiguationData":[OSD([sQuery(id+"F4.wireOp",EDGE,"E30")])]}),makeQuery(id+"F8.opExtrude","SWEPT_FACE",FACE,{"disambiguationData":[OSD([sQuery(id+"F7.wireOp",EDGE,"E67")])]})]});
            fillet(context, id + "F14", {"entities" : qUnion([Q0, Q1, Q2, Q3, Q4, Q5]), "radius" : 3 * mm, "tangentPropagation" : true, "allowEdgeOverflow" : false});
        }
        {
            var Q0;
            Q0=makeQuery(id+"F1.opExtrude","CAP_EDGE",EDGE,{"disambiguationData":[OSD([sQuery(id+"F0.wireOp",EDGE,"E1.bottom")])],"isStart":false});
            fillet(context, id + "F15", {"entities" : qUnion([Q0]), "radius" : 2 * mm, "tangentPropagation" : true, "allowEdgeOverflow" : false});
        }
        {
            var Q0;
            {var subQ0=sQuery(id+"F0.wireOp",EDGE,"E22.filletArc");var subQ1=sQuery(id+"F0.wireOp",EDGE,"E7");var subQ2=sQuery(id+"F0.wireOp",EDGE,"E6");var subQ3=sQuery(id+"F0.wireOp",EDGE,"E5");var subQ4=sQuery(id+"F0.wireOp",EDGE,"E4");var subQ5=sQuery(id+"F0.wireOp",EDGE,"E1.bottom");var subQ6=sQuery(id+"F0.wireOp",EDGE,"E21.filletArc");var subQ7=sQuery(id+"F0.wireOp",EDGE,"E1.top");var subQ8=sQuery(id+"F0.wireOp",EDGE,"E1.left");var subQ9=sQuery(id+"F0.wireOp",EDGE,"E1.right");var subQ10=sQuery(id+"F0.wireOp",EDGE,"E23.filletArc");var subQ11=sQuery(id+"F0.wireOp",EDGE,"E24.filletArc");Q0=makeQuery(id+"F2.boolean.opBoolean","SPLIT",FACE,{"disambiguationData":[TD([makeQuery(id+"F1.opExtrude","SWEPT_FACE",FACE,{"disambiguationData":[OSD([subQ5])]})])],"derivedFrom":makeQuery(id+"F1.opExtrude","CAP_FACE",FACE,{"disambiguationData":[OSD([subQ5,subQ7,subQ8,subQ9,subQ4,subQ3,subQ2,subQ1,subQ6,subQ0,subQ10,subQ11])],"isStart":true})});}
            var sketch = newSketch(context, id + "F16", { "sketchPlane" : qUnion([Q0])});
            skCircle(sketch, "E79", {"center": v(0, -165) * mm, "radius": 6 * mm});
            skArc(sketch, "E80", {"start": v(15, -164.85) * mm, "mid": v(0.56, -179.99) * mm, "end": v(-14.97, -165.96) * mm});
            skLineSegment(sketch, "E81", {"start": v(-14.97, -154.11) * mm, "end": v(-14.97, -165.96) * mm});
            skLineSegment(sketch, "E82", {"start": v(15, -153) * mm, "end": v(15, -164.85) * mm});
            skLineSegment(sketch, "E83", {"start": v(15, -153) * mm, "end": v(33, -135) * mm});
            skLineSegment(sketch, "E84", {"start": v(-14.97, -154.11) * mm, "end": v(-31.79, -135) * mm});
            skLineSegment(sketch, "E85", {"start": v(0, -165) * mm, "end": v(0, -135) * mm, "construction": true});
            skLineSegment(sketch, "E86.0", {"start": v(-70, -135) * mm, "end": v(70, -135) * mm});
            skLineSegment(sketch, "E87", {"start": v(-101.1, 0) * mm, "end": v(91.37, 0) * mm, "construction": true});
            skPoint(sketch, "E87.startSnap0", {"position": v(-60, 0) * mm});
            skPoint(sketch, "E87.endSnap0", {"position": v(-60, 0) * mm});
            skLineSegment(sketch, "E88.MirrorCS", {"start": v(-14.97, 154.11) * mm, "end": v(-31.79, 135) * mm});
            skLineSegment(sketch, "E89.MirrorCS", {"start": v(-14.97, 154.11) * mm, "end": v(-14.97, 165.96) * mm});
            skArc(sketch, "E90.MirrorCS", {"start": v(15, 164.85) * mm, "mid": v(0.56, 179.99) * mm, "end": v(-14.97, 165.96) * mm});
            skLineSegment(sketch, "E91.MirrorCS", {"start": v(15, 153) * mm, "end": v(15, 164.85) * mm});
            skLineSegment(sketch, "E92.MirrorCS", {"start": v(15, 153) * mm, "end": v(33, 135) * mm});
            skLineSegment(sketch, "E93.MirrorCS", {"start": v(0, 165) * mm, "end": v(0, 135) * mm, "construction": true});
            skCircle(sketch, "E94.MirrorC", {"center": v(0, 165) * mm, "radius": 6 * mm});
            skSolve(sketch);
        }
        {
            var Q0;
            {var subQ0=sQuery(id+"F16.wireOp",EDGE,"E88.MirrorCS");Q0=makeQuery(id+"F16.imprint","IMPRINT",FACE,{"disambiguationData":[TD([[makeQuery(id+"F16.imprint","IMPRINT",EDGE,{"derivedFrom":subQ0}),1.0]])]});}
            var Q1;
            Q1=makeQuery(id+"F16.imprint","IMPRINT",FACE,{"disambiguationData":[TD([[makeQuery(id+"F16.imprint","IMPRINT",EDGE,{"derivedFrom":sQuery(id+"F16.wireOp",EDGE,"E79")}),-1.0]])]});
            var Q2;
            Q2=makeQuery(id+"F16.imprint","IMPRINT",FACE,{"disambiguationData":[TD([[makeQuery(id+"F16.imprint","IMPRINT",EDGE,{"derivedFrom":makeQuery(id+"F1.opExtrude","CAP_EDGE",EDGE,{"disambiguationData":[OSD([sQuery(id+"F0.wireOp",EDGE,"E1.left")])],"isStart":true})}),-1.0]])]});
            var Q3;
            Q3=makeQuery(id+"F2.opExtrude","CAP_FACE",FACE,{"disambiguationData":[OSD([sQuery(id+"F0.wireOp",EDGE,"E12"),sQuery(id+"F0.wireOp",EDGE,"E13"),sQuery(id+"F0.wireOp",EDGE,"E14"),sQuery(id+"F0.wireOp",EDGE,"E15"),sQuery(id+"F0.wireOp",EDGE,"E17.filletArc"),sQuery(id+"F0.wireOp",EDGE,"E18.filletArc"),sQuery(id+"F0.wireOp",EDGE,"E19.filletArc"),sQuery(id+"F0.wireOp",EDGE,"E20.filletArc"),sQuery(id+"F0.wireOp",EDGE,"E25.0"),sQuery(id+"F0.wireOp",EDGE,"E25.1"),sQuery(id+"F0.wireOp",EDGE,"E25.2"),sQuery(id+"F0.wireOp",EDGE,"E25.3"),sQuery(id+"F0.wireOp",EDGE,"E25.4"),sQuery(id+"F0.wireOp",EDGE,"E25.5"),sQuery(id+"F0.wireOp",EDGE,"E25.6"),sQuery(id+"F0.wireOp",EDGE,"E25.7")])],"isStart":false});
            extrude(context, id + "F17", {"entities" : qUnion([Q0, Q1, Q2]), "endBound" : BoundingType.UP_TO_SURFACE, "endBoundEntityFace" : qUnion([Q3]), "depth" : 25 * mm});
        }
    });
